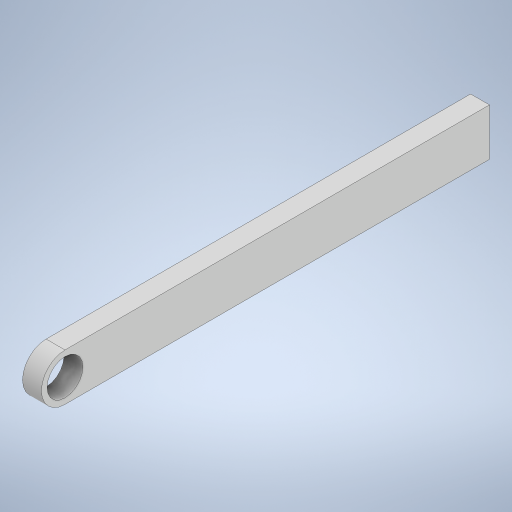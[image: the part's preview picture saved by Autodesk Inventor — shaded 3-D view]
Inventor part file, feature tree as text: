
AUTODESK INVENTOR PART (.ipt)
format: ipt  version: 2023 (Build 270158000, 158)  size: 227,328 bytes
history: native  units: mm
features: other x1, extrude x1, sketch x1
ambient origin geometry x8: Origin, YZ Plane, XZ Plane, XY Plane, X Axis, Y Axis, Z Axis, Center Point
bodies: Body1 (feature_tree)
feature tree (3):
  other  "Bryła1"
  extrude  "Wyciągnięcie proste1"  Depth=3.8mm
  sketch  "Szkic1"
